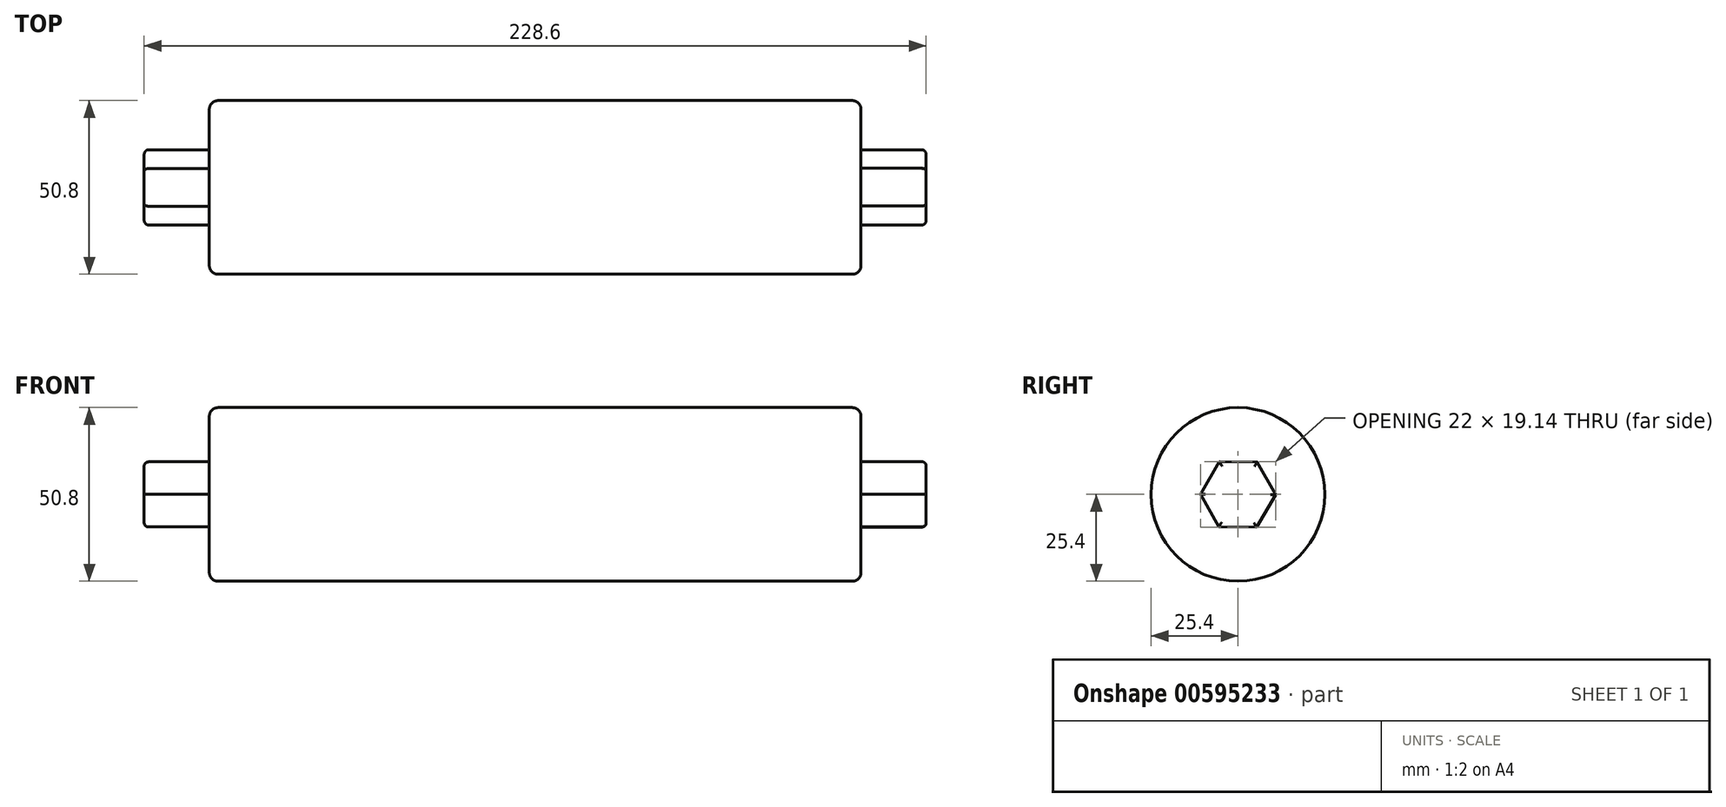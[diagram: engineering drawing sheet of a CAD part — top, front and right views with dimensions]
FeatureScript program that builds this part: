
annotation { "Feature Type Name" : "Feature", "Feature Type Description" : "" }
export const myFeature = defineFeature(function(context is Context, id is Id, definition is map)
    precondition{}
    {
        {
            var Q0;
            Q0=qCreatedBy(makeId("Right.planeOp"),FACE);
            var sketch = newSketch(context, id + "F0", { "sketchPlane" : qUnion([Q0])});
            skCircle(sketch, "E0", {"center": v(0, 0) * mm, "radius": 25.4 * mm});
            skSolve(sketch);
        }
        {
            var Q0;
            Q0=qSketchRegion(id+"F0",true);
            extrude(context, id + "F1", {"entities" : qUnion([Q0]), "depth" : 190.5 * mm});
        }
        {
            var Q0;
            Q0=makeQuery(id+"F1.opExtrude","CAP_FACE",FACE,{"disambiguationData":[OSD([sQuery(id+"F0.wireOp",EDGE,"E0")])],"isStart":true});
            var sketch = newSketch(context, id + "F2", { "sketchPlane" : qUnion([Q0])});
            skCircle(sketch, "E1.cCircle", {"center": v(0, 0) * mm, "radius": 9.53 * mm, "construction": true});
            skLineSegment(sketch, "E1.0", {"start": v(-5.5, 9.53) * mm, "end": v(5.5, 9.53) * mm});
            skLineSegment(sketch, "E1.1", {"start": v(5.5, 9.52) * mm, "end": v(11, 0) * mm});
            skLineSegment(sketch, "E1.2", {"start": v(11, 0) * mm, "end": v(5.5, -9.52) * mm});
            skLineSegment(sketch, "E1.3", {"start": v(5.5, -9.52) * mm, "end": v(-5.5, -9.53) * mm});
            skLineSegment(sketch, "E1.4", {"start": v(-5.5, -9.53) * mm, "end": v(-11, 0) * mm});
            skLineSegment(sketch, "E1.5", {"start": v(-11, 0) * mm, "end": v(-5.5, 9.52) * mm});
            skPoint(sketch, "E1.0.midPoint", {"position": v(0, 9.53) * mm});
            skSolve(sketch);
        }
        {
            var Q0;
            Q0=qSketchRegion(id+"F2",true);
            extrude(context, id + "F3", {"entities" : qUnion([Q0]), "operationType" : NewBodyOperationType.ADD, "depth" : 19.05 * mm});
        }
        {
            var Q0;
            Q0=makeQuery(id+"F1.opExtrude","CAP_FACE",FACE,{"disambiguationData":[OSD([sQuery(id+"F0.wireOp",EDGE,"E0")])],"isStart":false});
            var sketch = newSketch(context, id + "F4", { "sketchPlane" : qUnion([Q0])});
            skCircle(sketch, "E2.cCircle", {"center": v(0, 0) * mm, "radius": 9.53 * mm, "construction": true});
            skLineSegment(sketch, "E2.0", {"start": v(5.58, 9.48) * mm, "end": v(11, -0.1) * mm});
            skLineSegment(sketch, "E2.1", {"start": v(11, -0.1) * mm, "end": v(5.42, -9.57) * mm});
            skLineSegment(sketch, "E2.2", {"start": v(5.42, -9.57) * mm, "end": v(-5.58, -9.48) * mm});
            skLineSegment(sketch, "E2.3", {"start": v(-5.58, -9.48) * mm, "end": v(-11, 0.1) * mm});
            skLineSegment(sketch, "E2.4", {"start": v(-11, 0.1) * mm, "end": v(-5.42, 9.57) * mm});
            skLineSegment(sketch, "E2.5", {"start": v(-5.42, 9.57) * mm, "end": v(5.58, 9.48) * mm});
            skPoint(sketch, "E2.0.midPoint", {"position": v(8.29, 4.7) * mm});
            skSolve(sketch);
        }
        {
            var Q0;
            Q0=qSketchRegion(id+"F4",true);
            extrude(context, id + "F5", {"entities" : qUnion([Q0]), "operationType" : NewBodyOperationType.ADD, "depth" : 19.05 * mm});
        }
        {
            var Q0;
            Q0=makeQuery(id+"F1.opExtrude","CAP_EDGE",EDGE,{"disambiguationData":[OSD([sQuery(id+"F0.wireOp",EDGE,"E0")])],"isStart":false});
            fillet(context, id + "F6", {"entities" : qUnion([Q0]), "radius" : 2.54 * mm, "tangentPropagation" : true, "allowEdgeOverflow" : false});
        }
        {
            var Q0;
            Q0=makeQuery(id+"F1.opExtrude","CAP_EDGE",EDGE,{"disambiguationData":[OSD([sQuery(id+"F0.wireOp",EDGE,"E0")])],"isStart":true});
            fillet(context, id + "F7", {"entities" : qUnion([Q0]), "radius" : 2.54 * mm, "tangentPropagation" : true, "allowEdgeOverflow" : false});
        }
        {
            var Q0;
            Q0=makeQuery(id+"F5.opExtrude","CAP_FACE",FACE,{"disambiguationData":[OSD([sQuery(id+"F4.wireOp",EDGE,"E2.0"),sQuery(id+"F4.wireOp",EDGE,"E2.1"),sQuery(id+"F4.wireOp",EDGE,"E2.2"),sQuery(id+"F4.wireOp",EDGE,"E2.3"),sQuery(id+"F4.wireOp",EDGE,"E2.4"),sQuery(id+"F4.wireOp",EDGE,"E2.5")])],"isStart":false});
            fillet(context, id + "F8", {"entities" : qUnion([Q0]), "radius" : 1.27 * mm, "tangentPropagation" : true, "allowEdgeOverflow" : false});
        }
        {
            var Q0;
            Q0=makeQuery(id+"F3.opExtrude","CAP_FACE",FACE,{"disambiguationData":[OSD([sQuery(id+"F2.wireOp",EDGE,"E1.0"),sQuery(id+"F2.wireOp",EDGE,"E1.1"),sQuery(id+"F2.wireOp",EDGE,"E1.2"),sQuery(id+"F2.wireOp",EDGE,"E1.3"),sQuery(id+"F2.wireOp",EDGE,"E1.4"),sQuery(id+"F2.wireOp",EDGE,"E1.5")])],"isStart":false});
            fillet(context, id + "F9", {"entities" : qUnion([Q0]), "radius" : 1.27 * mm, "tangentPropagation" : true, "allowEdgeOverflow" : false});
        }
    });
